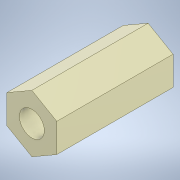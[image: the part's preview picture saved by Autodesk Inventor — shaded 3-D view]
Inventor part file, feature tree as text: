
AUTODESK INVENTOR PART (.ipt)
format: ipt  version: 2020.2 (Build 242310000, 310)  size: 99,840 bytes
history: native  units: mm
features: other x1, extrude x1, sketch x1
ambient origin geometry x8: Origin, YZ Plane, XZ Plane, XY Plane, X Axis, Y Axis, Z Axis, Center Point
bodies: Body1 (feature_tree)
feature tree (3):
  other  "ソリッド1"
  extrude  "押し出し1"  Depth=6.0mm
  sketch  "スケッチ1"
